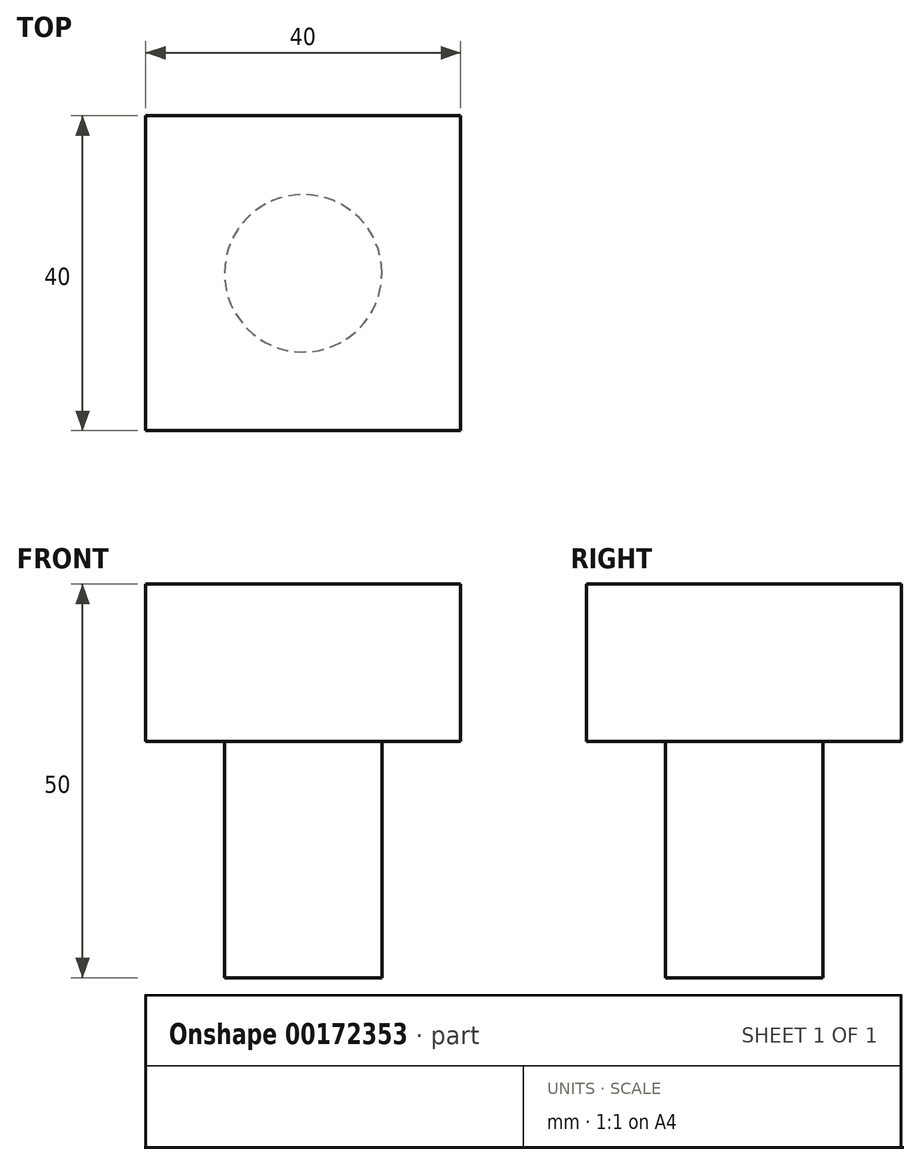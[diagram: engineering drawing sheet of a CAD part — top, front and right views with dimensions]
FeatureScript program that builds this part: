
annotation { "Feature Type Name" : "Feature", "Feature Type Description" : "" }
export const myFeature = defineFeature(function(context is Context, id is Id, definition is map)
    precondition{}
    {
        {
            var Q0;
            Q0=qCreatedBy(makeId("Top.planeOp"),FACE);
            var sketch = newSketch(context, id + "F0", { "sketchPlane" : qUnion([Q0])});
            skLineSegment(sketch, "E0.bottom", {"start": v(20, 20) * mm, "end": v(-20, 20) * mm});
            skLineSegment(sketch, "E0.top", {"start": v(20, -20) * mm, "end": v(-20, -20) * mm});
            skLineSegment(sketch, "E0.left", {"start": v(20, 20) * mm, "end": v(20, -20) * mm});
            skLineSegment(sketch, "E0.right", {"start": v(-20, 20) * mm, "end": v(-20, -20) * mm});
            skPoint(sketch, "E0.middle", {"position": v(0, 0) * mm});
            skSolve(sketch);
        }
        {
            var Q0;
            Q0=qSketchRegion(id+"F0",true);
            extrude(context, id + "F1", {"entities" : qUnion([Q0]), "depth" : 20 * mm});
        }
        {
            var Q0;
            Q0=makeQuery(id+"F1.opExtrude","CAP_FACE",FACE,{"disambiguationData":[OSD([sQuery(id+"F0.wireOp",EDGE,"E0.bottom"),sQuery(id+"F0.wireOp",EDGE,"E0.top"),sQuery(id+"F0.wireOp",EDGE,"E0.left"),sQuery(id+"F0.wireOp",EDGE,"E0.right")])],"isStart":false});
            var sketch = newSketch(context, id + "F2", { "sketchPlane" : qUnion([Q0])});
            skCircle(sketch, "E1", {"center": v(0, 0) * mm, "radius": 10 * mm});
            skSolve(sketch);
        }
        {
            var Q0;
            Q0=qSketchRegion(id+"F2",true);
            extrude(context, id + "F3", {"entities" : qUnion([Q0]), "operationType" : NewBodyOperationType.ADD, "oppositeDirection" : true, "depth" : 50 * mm});
        }
    });
